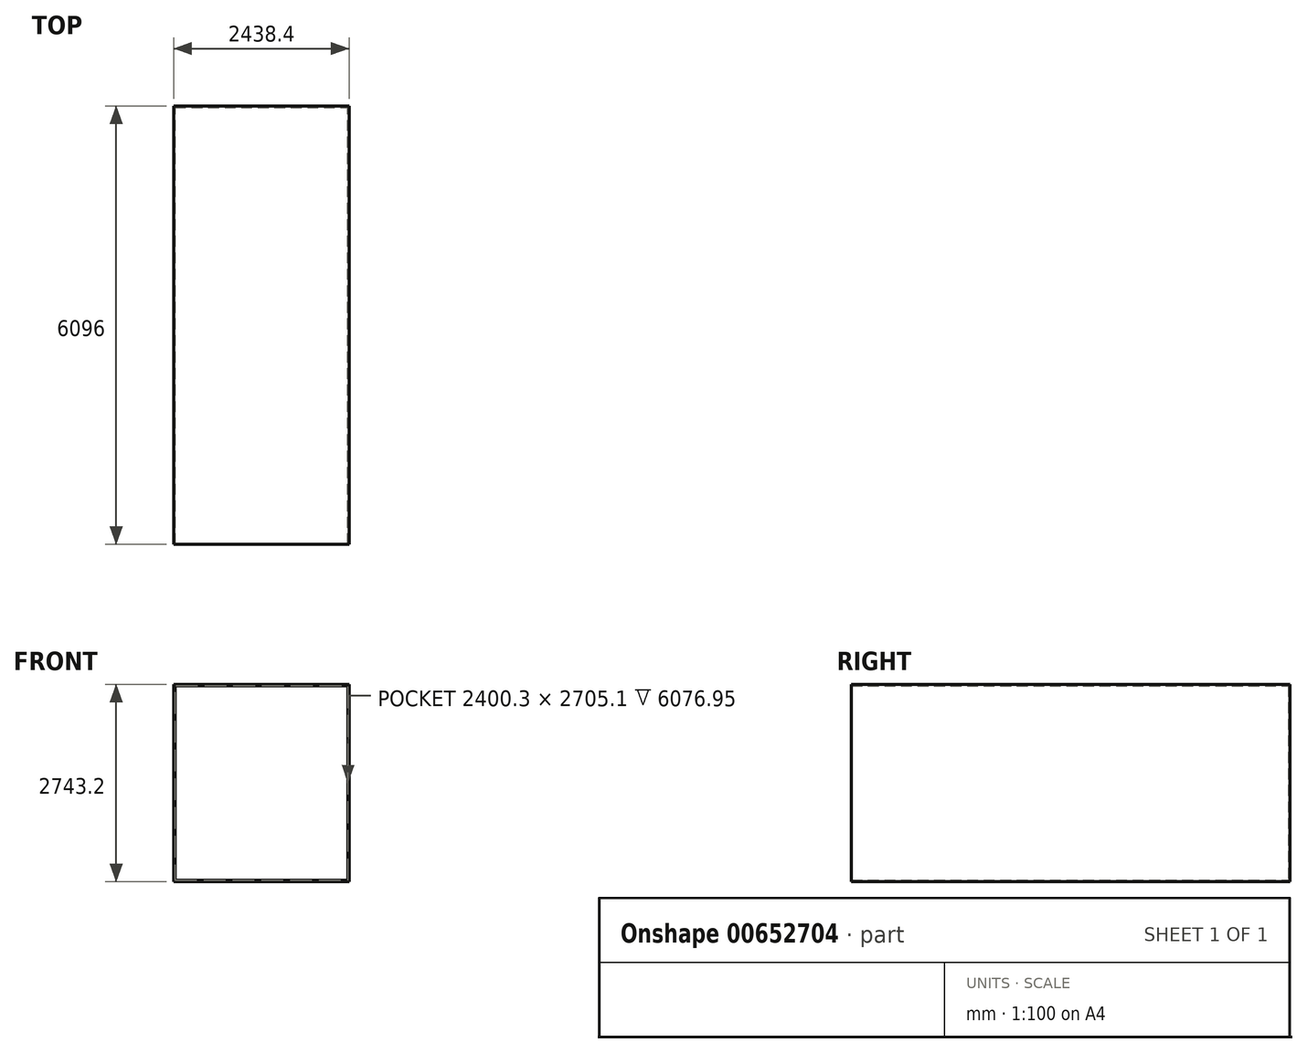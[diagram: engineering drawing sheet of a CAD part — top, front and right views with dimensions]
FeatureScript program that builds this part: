
annotation { "Feature Type Name" : "Feature", "Feature Type Description" : "" }
export const myFeature = defineFeature(function(context is Context, id is Id, definition is map)
    precondition{}
    {
        {
            var Q0;
            Q0=qCreatedBy(makeId("Front.planeOp"),FACE);
            var sketch = newSketch(context, id + "F0", { "sketchPlane" : qUnion([Q0])});
            skLineSegment(sketch, "E0.bottom", {"start": v(-1219.2, 1371.6) * mm, "end": v(1219.2, 1371.6) * mm});
            skLineSegment(sketch, "E0.top", {"start": v(-1219.2, -1371.6) * mm, "end": v(1219.2, -1371.6) * mm});
            skLineSegment(sketch, "E0.left", {"start": v(-1219.2, 1371.6) * mm, "end": v(-1219.2, -1371.6) * mm});
            skLineSegment(sketch, "E0.right", {"start": v(1219.2, 1371.6) * mm, "end": v(1219.2, -1371.6) * mm});
            skSolve(sketch);
        }
        {
            var Q0;
            Q0 = qSketchRegion(id + "F0", true);
            extrude(context, id + "F1", {"entities" : qUnion([Q0]), "endBound" : BoundingType.SYMMETRIC, "depth" : 6096 * mm, "offsetDistance" : 25.4 * mm});
        }
        {
            var Q0;
            Q0=makeQuery(id+"F1.opExtrude","CAP_FACE",FACE,{"disambiguationData":[OSD([sQuery(id+"F0.wireOp",EDGE,"E0.bottom"),sQuery(id+"F0.wireOp",EDGE,"E0.top"),sQuery(id+"F0.wireOp",EDGE,"E0.left"),sQuery(id+"F0.wireOp",EDGE,"E0.right")])],"isStart":false});
            shell(context, id + "F2", {"entities" : qUnion([Q0]), "thickness" : 19.05 * mm});
        }
    });
